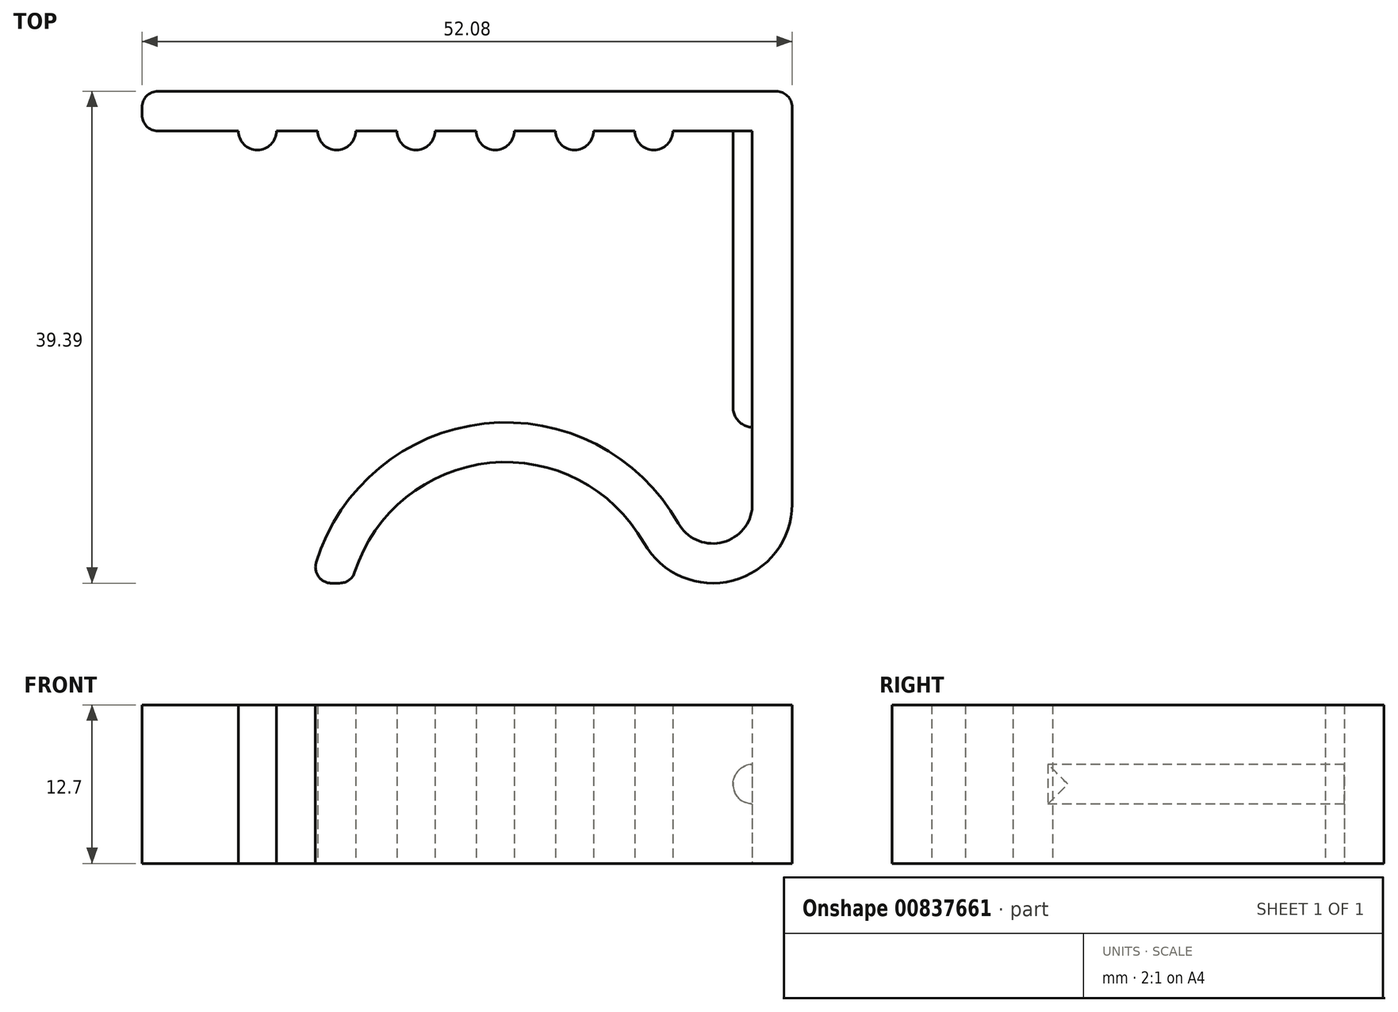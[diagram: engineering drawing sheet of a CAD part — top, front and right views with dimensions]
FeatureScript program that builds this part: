
annotation { "Feature Type Name" : "Feature", "Feature Type Description" : "" }
export const myFeature = defineFeature(function(context is Context, id is Id, definition is map)
    precondition{}
    {
        {
            var Q0;
            Q0=qCreatedBy(makeId("Top.planeOp"),FACE);
            var sketch = newSketch(context, id + "F0", { "sketchPlane" : qUnion([Q0])});
            skLineSegment(sketch, "E0", {"start": v(17.73, 11) * mm, "end": v(17.73, -12.73) * mm});
            skLineSegment(sketch, "E1.1", {"start": v(19.25, 11) * mm, "end": v(19.25, -19.33) * mm});
            skLineSegment(sketch, "E1.2", {"start": v(-29.62, 11) * mm, "end": v(-21.9, 11) * mm});
            skArc(sketch, "E2", {"start": v(3.5, 11) * mm, "mid": v(5.03, 9.47) * mm, "end": v(6.55, 11) * mm});
            skArc(sketch, "E3", {"start": v(9.85, 11) * mm, "mid": v(11.38, 9.47) * mm, "end": v(12.9, 11) * mm});
            skArc(sketch, "E4", {"start": v(-2.85, 11) * mm, "mid": v(-1.32, 9.47) * mm, "end": v(0.2, 11) * mm});
            skArc(sketch, "E5", {"start": v(-9.2, 11) * mm, "mid": v(-7.67, 9.47) * mm, "end": v(-6.15, 11) * mm});
            skArc(sketch, "E6", {"start": v(-15.55, 11) * mm, "mid": v(-14.02, 9.47) * mm, "end": v(-12.5, 11) * mm});
            skArc(sketch, "E7", {"start": v(-21.9, 11) * mm, "mid": v(-20.37, 9.47) * mm, "end": v(-18.85, 11) * mm});
            skLineSegment(sketch, "E8", {"start": v(-29.62, 11) * mm, "end": v(-29.62, 14.17) * mm});
            skLineSegment(sketch, "E9", {"start": v(-29.62, 14.17) * mm, "end": v(22.46, 14.17) * mm});
            skLineSegment(sketch, "E10", {"start": v(22.46, 14.17) * mm, "end": v(22.46, -18.87) * mm});
            skLineSegment(sketch, "E11.trimOffspring", {"start": v(12.9, 11) * mm, "end": v(19.25, 11) * mm});
            skLineSegment(sketch, "E12.trimOffspring", {"start": v(6.55, 11) * mm, "end": v(9.85, 11) * mm});
            skLineSegment(sketch, "E13.trimOffspring", {"start": v(0.2, 11) * mm, "end": v(3.5, 11) * mm});
            skLineSegment(sketch, "E14.trimOffspring", {"start": v(-6.15, 11) * mm, "end": v(-2.85, 11) * mm});
            skLineSegment(sketch, "E15.trimOffspring", {"start": v(-12.5, 11) * mm, "end": v(-9.2, 11) * mm});
            skLineSegment(sketch, "E16.trimOffspring", {"start": v(-18.85, 11) * mm, "end": v(-15.55, 11) * mm});
            skArc(sketch, "E17", {"start": v(10.58, -22) * mm, "mid": v(17.72, -25.01) * mm, "end": v(22.46, -18.87) * mm});
            skArc(sketch, "E18", {"start": v(10.6, -22.05) * mm, "mid": v(-2.2, -15.64) * mm, "end": v(-12.83, -25.22) * mm});
            skLineSegment(sketch, "E19.trimOffspring", {"start": v(-12.83, -25.22) * mm, "end": v(-16.08, -25.22) * mm});
            skArc(sketch, "E20.0", {"start": v(13.38, -20.5) * mm, "mid": v(-3, -12.55) * mm, "end": v(-16.08, -25.22) * mm});
            skArc(sketch, "E21.0", {"start": v(13.34, -20.43) * mm, "mid": v(16.69, -22) * mm, "end": v(19.25, -19.33) * mm});
            skLineSegment(sketch, "E22", {"start": v(17.73, -12.73) * mm, "end": v(19.25, -12.73) * mm});
            skSolve(sketch);
        }
        {
            var Q0;
            Q0=makeQuery(id+"F0.imprint","IMPRINT",FACE,{"disambiguationData":[TD([[makeQuery(id+"F0.imprint","IMPRINT",EDGE,{"derivedFrom":sQuery(id+"F0.wireOp",EDGE,"E1.2")}),1.0]])]});
            extrude(context, id + "F1", {"entities" : qUnion([Q0]), "depth" : 12.7 * mm, "offsetDistance" : 25.4 * mm});
        }
        {
            var Q0;
            {var subQ0=sQuery(id+"F0.wireOp",EDGE,"E0");Q0=makeQuery(id+"F0.imprint","IMPRINT",FACE,{"disambiguationData":[TD([[makeQuery(id+"F0.imprint","IMPRINT",EDGE,{"derivedFrom":subQ0}),1.0]])]});}
            extrude(context, id + "F2", {"entities" : qUnion([Q0]), "operationType" : NewBodyOperationType.ADD, "depth" : 7.94 * mm, "offsetDistance" : 25.4 * mm, "hasSecondDirection" : true, "secondDirectionOppositeDirection" : false, "secondDirectionDepth" : 4.76 * mm});
        }
        {
            var Q0;
            Q0=makeQuery(id+"F1.opExtrude","SWEPT_EDGE",EDGE,{"disambiguationData":[OSD([sQuery(id+"F0.wireOp",EDGE,"E19.trimOffspring"),sQuery(id+"F0.wireOp",EDGE,"E20.0")])]});
            var Q1;
            Q1=makeQuery(id+"F1.opExtrude","SWEPT_EDGE",EDGE,{"disambiguationData":[OSD([sQuery(id+"F0.wireOp",EDGE,"E18"),sQuery(id+"F0.wireOp",EDGE,"E19.trimOffspring")])]});
            var Q2;
            Q2=makeQuery(id+"F1.opExtrude","SWEPT_EDGE",EDGE,{"disambiguationData":[OSD([sQuery(id+"F0.wireOp",EDGE,"E8"),sQuery(id+"F0.wireOp",EDGE,"E9")])]});
            var Q3;
            Q3=makeQuery(id+"F1.opExtrude","SWEPT_EDGE",EDGE,{"disambiguationData":[OSD([sQuery(id+"F0.wireOp",EDGE,"E1.2"),sQuery(id+"F0.wireOp",EDGE,"E8")])]});
            var Q4;
            Q4=makeQuery(id+"F1.opExtrude","SWEPT_EDGE",EDGE,{"disambiguationData":[OSD([sQuery(id+"F0.wireOp",EDGE,"E9"),sQuery(id+"F0.wireOp",EDGE,"E10")])]});
            fillet(context, id + "F3", {"entities" : qUnion([Q0, Q1, Q2, Q3, Q4]), "radius" : 1.27 * mm, "tangentPropagation" : true, "allowEdgeOverflow" : false});
        }
        {
            var Q0;
            Q0=makeQuery(id+"F2.opExtrude","CAP_EDGE",EDGE,{"disambiguationData":[OSD([sQuery(id+"F0.wireOp",EDGE,"E0")])],"isStart":false});
            var Q1;
            Q1=makeQuery(id+"F2.opExtrude","CAP_EDGE",EDGE,{"disambiguationData":[OSD([sQuery(id+"F0.wireOp",EDGE,"E0")])],"isStart":true});
            var Q2;
            Q2=makeQuery(id+"F2.opExtrude","SWEPT_EDGE",EDGE,{"disambiguationData":[OSD([sQuery(id+"F0.wireOp",EDGE,"E0"),sQuery(id+"F0.wireOp",EDGE,"E22")])]});
            fillet(context, id + "F4", {"entities" : qUnion([Q0, Q1, Q2]), "radius" : 1.57 * mm, "tangentPropagation" : true, "allowEdgeOverflow" : false});
        }
    });
